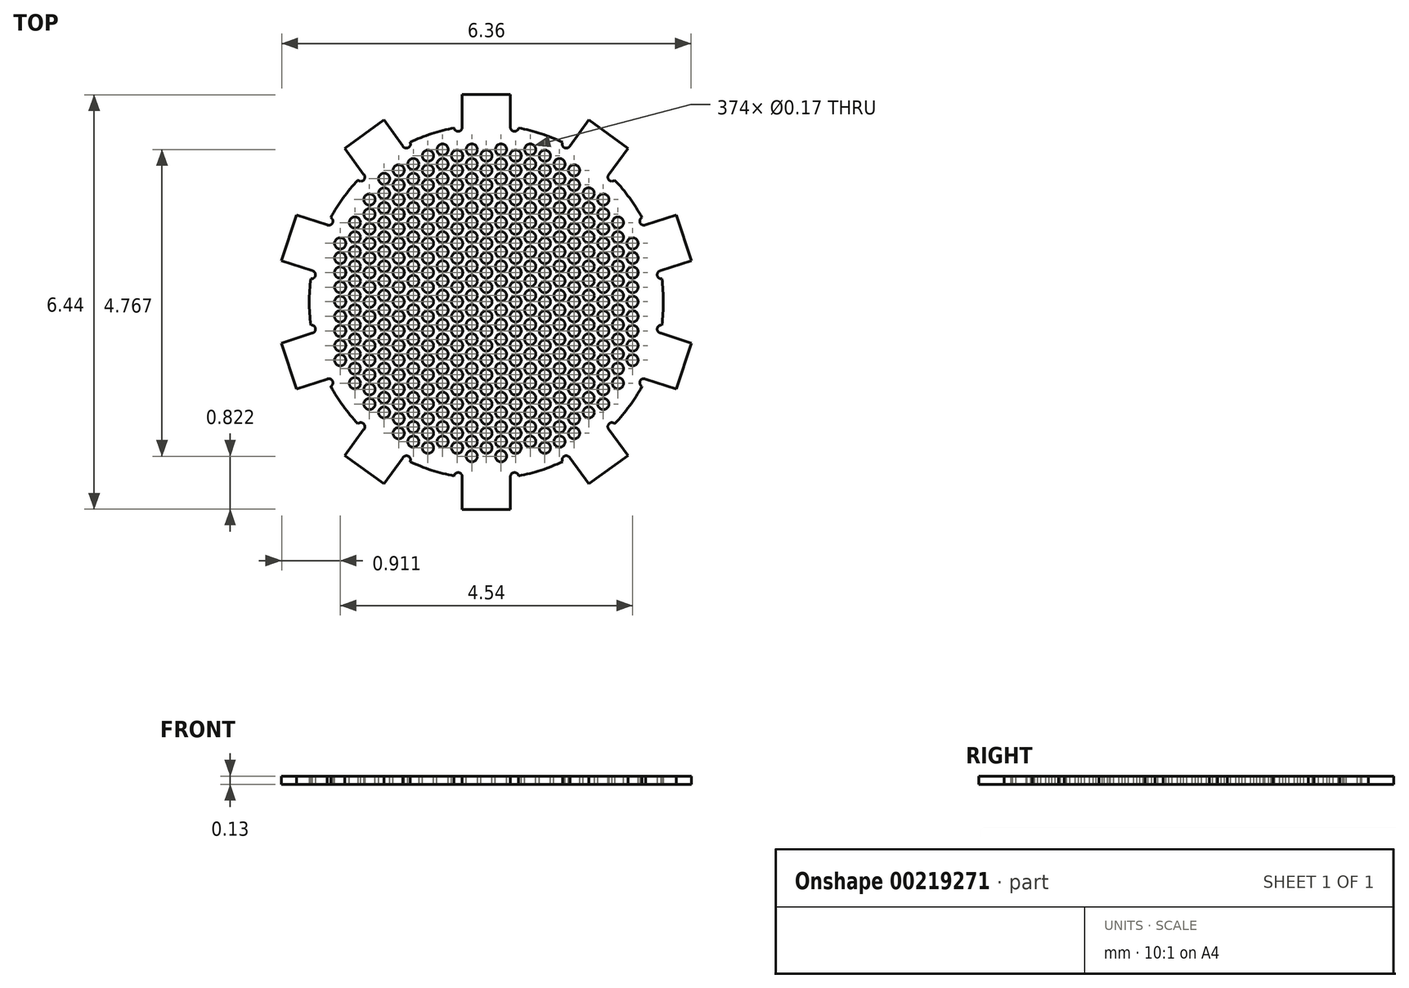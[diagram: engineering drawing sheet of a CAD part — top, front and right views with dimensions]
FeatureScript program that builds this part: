
annotation { "Feature Type Name" : "Feature", "Feature Type Description" : "" }
export const myFeature = defineFeature(function(context is Context, id is Id, definition is map)
    precondition{}
    {
        {
            var Q0;
            Q0=qCreatedBy(makeId("Top.planeOp"),FACE);
            var sketch = newSketch(context, id + "F0", { "sketchPlane" : qUnion([Q0])});
            skCircle(sketch, "E0", {"center": v(0, 0) * mm, "radius": 2.5 * mm});
            skArc(sketch, "E1", {"start": v(0.37, 2.72) * mm, "mid": v(0, 2.75) * mm, "end": v(-0.38, 2.72) * mm});
            skLineSegment(sketch, "E2", {"start": v(-0.37, 2.72) * mm, "end": v(-0.37, 3.22) * mm});
            skLineSegment(sketch, "E3", {"start": v(-0.38, 3.22) * mm, "end": v(0.38, 3.22) * mm});
            skLineSegment(sketch, "E4", {"start": v(0.38, 3.22) * mm, "end": v(0.38, 2.72) * mm});
            skArc(sketch, "E5", {"start": v(-0.5, 2.7) * mm, "mid": v(-0.43, 2.65) * mm, "end": v(-0.38, 2.72) * mm});
            skArc(sketch, "E6", {"start": v(0.38, 2.72) * mm, "mid": v(0.43, 2.65) * mm, "end": v(0.5, 2.7) * mm});
            skArc(sketch, "E7.trimOffspring", {"start": v(-0.5, 2.7) * mm, "mid": v(-0.85, 2.62) * mm, "end": v(-1.18, 2.48) * mm});
            skArc(sketch, "E8.1.0", {"start": v(-2, 1.9) * mm, "mid": v(-1.9, 1.9) * mm, "end": v(-1.9, 1.98) * mm});
            skLineSegment(sketch, "E8.1.1", {"start": v(-1.9, 1.98) * mm, "end": v(-2.2, 2.39) * mm});
            skLineSegment(sketch, "E8.1.2", {"start": v(-2.2, 2.39) * mm, "end": v(-1.6, 2.83) * mm});
            skArc(sketch, "E8.1.3", {"start": v(-1.3, 2.42) * mm, "mid": v(-1.21, 2.4) * mm, "end": v(-1.18, 2.48) * mm});
            skLineSegment(sketch, "E8.1.4", {"start": v(-1.6, 2.83) * mm, "end": v(-1.3, 2.42) * mm});
            skArc(sketch, "E8.2.0", {"start": v(-2.73, 0.36) * mm, "mid": v(-2.65, 0.41) * mm, "end": v(-2.7, 0.49) * mm});
            skLineSegment(sketch, "E8.2.1", {"start": v(-2.7, 0.49) * mm, "end": v(-3.18, 0.64) * mm});
            skLineSegment(sketch, "E8.2.2", {"start": v(-3.18, 0.64) * mm, "end": v(-2.95, 1.35) * mm});
            skArc(sketch, "E8.2.3", {"start": v(-2.48, 1.2) * mm, "mid": v(-2.4, 1.23) * mm, "end": v(-2.42, 1.31) * mm});
            skLineSegment(sketch, "E8.2.4", {"start": v(-2.95, 1.35) * mm, "end": v(-2.48, 1.2) * mm});
            skArc(sketch, "E8.3.0", {"start": v(-2.42, -1.31) * mm, "mid": v(-2.4, -1.23) * mm, "end": v(-2.48, -1.2) * mm});
            skLineSegment(sketch, "E8.3.1", {"start": v(-2.48, -1.2) * mm, "end": v(-2.95, -1.35) * mm});
            skLineSegment(sketch, "E8.3.2", {"start": v(-2.95, -1.35) * mm, "end": v(-3.18, -0.64) * mm});
            skArc(sketch, "E8.3.3", {"start": v(-2.7, -0.49) * mm, "mid": v(-2.65, -0.41) * mm, "end": v(-2.73, -0.36) * mm});
            skLineSegment(sketch, "E8.3.4", {"start": v(-3.18, -0.64) * mm, "end": v(-2.7, -0.49) * mm});
            skArc(sketch, "E8.4.0", {"start": v(-1.18, -2.48) * mm, "mid": v(-1.21, -2.4) * mm, "end": v(-1.3, -2.42) * mm});
            skLineSegment(sketch, "E8.4.1", {"start": v(-1.3, -2.42) * mm, "end": v(-1.6, -2.83) * mm});
            skLineSegment(sketch, "E8.4.2", {"start": v(-1.6, -2.83) * mm, "end": v(-2.2, -2.39) * mm});
            skArc(sketch, "E8.4.3", {"start": v(-1.9, -1.98) * mm, "mid": v(-1.9, -1.9) * mm, "end": v(-2, -1.9) * mm});
            skLineSegment(sketch, "E8.4.4", {"start": v(-2.2, -2.39) * mm, "end": v(-1.9, -1.98) * mm});
            skArc(sketch, "E8.5.0", {"start": v(0.5, -2.7) * mm, "mid": v(0.43, -2.65) * mm, "end": v(0.37, -2.72) * mm});
            skLineSegment(sketch, "E8.5.1", {"start": v(0.37, -2.72) * mm, "end": v(0.37, -3.22) * mm});
            skLineSegment(sketch, "E8.5.2", {"start": v(0.37, -3.22) * mm, "end": v(-0.38, -3.22) * mm});
            skArc(sketch, "E8.5.3", {"start": v(-0.38, -2.72) * mm, "mid": v(-0.43, -2.65) * mm, "end": v(-0.5, -2.7) * mm});
            skLineSegment(sketch, "E8.5.4", {"start": v(-0.38, -3.22) * mm, "end": v(-0.38, -2.72) * mm});
            skArc(sketch, "E8.6.0", {"start": v(2, -1.9) * mm, "mid": v(1.9, -1.9) * mm, "end": v(1.9, -1.98) * mm});
            skLineSegment(sketch, "E8.6.1", {"start": v(1.9, -1.98) * mm, "end": v(2.2, -2.39) * mm});
            skLineSegment(sketch, "E8.6.2", {"start": v(2.2, -2.39) * mm, "end": v(1.6, -2.83) * mm});
            skArc(sketch, "E8.6.3", {"start": v(1.3, -2.42) * mm, "mid": v(1.21, -2.4) * mm, "end": v(1.18, -2.48) * mm});
            skLineSegment(sketch, "E8.6.4", {"start": v(1.6, -2.83) * mm, "end": v(1.3, -2.42) * mm});
            skArc(sketch, "E8.7.0", {"start": v(2.73, -0.36) * mm, "mid": v(2.65, -0.41) * mm, "end": v(2.7, -0.49) * mm});
            skLineSegment(sketch, "E8.7.1", {"start": v(2.7, -0.49) * mm, "end": v(3.18, -0.64) * mm});
            skLineSegment(sketch, "E8.7.2", {"start": v(3.18, -0.64) * mm, "end": v(2.95, -1.35) * mm});
            skArc(sketch, "E8.7.3", {"start": v(2.48, -1.2) * mm, "mid": v(2.4, -1.23) * mm, "end": v(2.42, -1.31) * mm});
            skLineSegment(sketch, "E8.7.4", {"start": v(2.95, -1.35) * mm, "end": v(2.48, -1.2) * mm});
            skArc(sketch, "E8.8.0", {"start": v(2.42, 1.31) * mm, "mid": v(2.4, 1.23) * mm, "end": v(2.48, 1.2) * mm});
            skLineSegment(sketch, "E8.8.1", {"start": v(2.48, 1.2) * mm, "end": v(2.95, 1.35) * mm});
            skLineSegment(sketch, "E8.8.2", {"start": v(2.95, 1.35) * mm, "end": v(3.18, 0.64) * mm});
            skArc(sketch, "E8.8.3", {"start": v(2.7, 0.49) * mm, "mid": v(2.65, 0.41) * mm, "end": v(2.73, 0.36) * mm});
            skLineSegment(sketch, "E8.8.4", {"start": v(3.18, 0.64) * mm, "end": v(2.7, 0.49) * mm});
            skArc(sketch, "E8.9.0", {"start": v(1.18, 2.48) * mm, "mid": v(1.21, 2.4) * mm, "end": v(1.3, 2.42) * mm});
            skLineSegment(sketch, "E8.9.1", {"start": v(1.3, 2.42) * mm, "end": v(1.6, 2.83) * mm});
            skLineSegment(sketch, "E8.9.2", {"start": v(1.6, 2.83) * mm, "end": v(2.2, 2.39) * mm});
            skArc(sketch, "E8.9.3", {"start": v(1.9, 1.98) * mm, "mid": v(1.9, 1.9) * mm, "end": v(2, 1.9) * mm});
            skLineSegment(sketch, "E8.9.4", {"start": v(2.2, 2.39) * mm, "end": v(1.9, 1.98) * mm});
            skArc(sketch, "E9.trimOffspring", {"start": v(1.18, 2.48) * mm, "mid": v(0.85, 2.62) * mm, "end": v(0.5, 2.7) * mm});
            skArc(sketch, "E10.trimOffspring", {"start": v(1.9, 1.98) * mm, "mid": v(1.62, 2.22) * mm, "end": v(1.3, 2.42) * mm});
            skArc(sketch, "E11.trimOffspring", {"start": v(2.42, 1.31) * mm, "mid": v(2.22, 1.62) * mm, "end": v(2, 1.9) * mm});
            skArc(sketch, "E12.trimOffspring", {"start": v(2.7, 0.49) * mm, "mid": v(2.62, 0.85) * mm, "end": v(2.48, 1.2) * mm});
            skArc(sketch, "E13.trimOffspring", {"start": v(2.73, -0.36) * mm, "mid": v(2.75, 0) * mm, "end": v(2.73, 0.36) * mm});
            skArc(sketch, "E14.trimOffspring", {"start": v(2.48, -1.2) * mm, "mid": v(2.62, -0.85) * mm, "end": v(2.7, -0.49) * mm});
            skArc(sketch, "E15.trimOffspring", {"start": v(2, -1.9) * mm, "mid": v(2.22, -1.62) * mm, "end": v(2.42, -1.31) * mm});
            skArc(sketch, "E16.trimOffspring", {"start": v(1.3, -2.42) * mm, "mid": v(1.62, -2.22) * mm, "end": v(1.9, -1.98) * mm});
            skArc(sketch, "E17.trimOffspring", {"start": v(0.44, -2.71) * mm, "mid": v(0.82, -2.63) * mm, "end": v(1.18, -2.48) * mm});
            skArc(sketch, "E18.trimOffspring", {"start": v(-1.24, -2.45) * mm, "mid": v(-0.88, -2.6) * mm, "end": v(-0.5, -2.7) * mm});
            skArc(sketch, "E19.trimOffspring", {"start": v(-2.42, -1.31) * mm, "mid": v(-2.22, -1.62) * mm, "end": v(-2, -1.9) * mm});
            skArc(sketch, "E20.trimOffspring", {"start": v(-2.7, -0.49) * mm, "mid": v(-2.62, -0.85) * mm, "end": v(-2.48, -1.2) * mm});
            skArc(sketch, "E21.trimOffspring", {"start": v(-2.73, 0.36) * mm, "mid": v(-2.75, 0) * mm, "end": v(-2.73, -0.36) * mm});
            skArc(sketch, "E22.trimOffspring", {"start": v(-2.48, 1.2) * mm, "mid": v(-2.62, 0.85) * mm, "end": v(-2.7, 0.49) * mm});
            skArc(sketch, "E23.trimOffspring", {"start": v(-2, 1.9) * mm, "mid": v(-2.22, 1.62) * mm, "end": v(-2.42, 1.31) * mm});
            skArc(sketch, "E24.trimOffspring", {"start": v(-1.3, 2.42) * mm, "mid": v(-1.62, 2.22) * mm, "end": v(-1.9, 1.98) * mm});
            skSolve(sketch);
        }
        {
            var Q0;
            Q0=qSketchRegion(id+"F0",true);
            var Q1;
            Q1=makeQuery(id+"F0.imprint","IMPRINT",FACE,{"disambiguationData":[TD([[makeQuery(id+"F0.imprint","IMPRINT",EDGE,{"derivedFrom":sQuery(id+"F0.wireOp",EDGE,"E0")}),1.0]])]});
            extrude(context, id + "F1", {"entities" : qUnion([Q0, Q1]), "depth" : 0.13 * mm});
        }
        {
            var Q0;
            Q0=makeQuery(id+"F1.opExtrude","CAP_FACE",FACE,{"disambiguationData":[OSD([sQuery(id+"F0.wireOp",EDGE,"E2"),sQuery(id+"F0.wireOp",EDGE,"E3"),sQuery(id+"F0.wireOp",EDGE,"E4"),sQuery(id+"F0.wireOp",EDGE,"E5"),sQuery(id+"F0.wireOp",EDGE,"E6"),sQuery(id+"F0.wireOp",EDGE,"E7.trimOffspring")])],"isStart":false});
            cPlane(context, id + "F2", {"entities" : qUnion([Q0]), "cplaneType" : CPlaneType.OFFSET, "offset" : 0 * mm, "width" : 150 * mm, "height" : 150 * mm});
        }
        {
            var Q0;
            Q0=qCreatedBy(id+"F2.planeOp",FACE);
            var sketch = newSketch(context, id + "F3", { "sketchPlane" : qUnion([Q0])});
            skCircle(sketch, "E25.2.1.8", {"center": v(-2.04, 1.23) * mm, "radius": 0.09 * mm});
            skCircle(sketch, "E25.2.1.9", {"center": v(-2.04, 1) * mm, "radius": 0.09 * mm});
            skCircle(sketch, "E25.0.1.10", {"center": v(-2.27, 0.91) * mm, "radius": 0.09 * mm});
            skCircle(sketch, "E25.2.1.10", {"center": v(-2.04, 0.78) * mm, "radius": 0.09 * mm});
            skCircle(sketch, "E25.2.2.5", {"center": v(-1.59, 1.91) * mm, "radius": 0.09 * mm});
            skCircle(sketch, "E25.2.2.6", {"center": v(-1.59, 1.69) * mm, "radius": 0.09 * mm});
            skCircle(sketch, "E25.0.2.7", {"center": v(-1.82, 1.6) * mm, "radius": 0.09 * mm});
            skCircle(sketch, "E25.2.2.7", {"center": v(-1.59, 1.46) * mm, "radius": 0.09 * mm});
            skCircle(sketch, "E25.0.2.8", {"center": v(-1.82, 1.36) * mm, "radius": 0.09 * mm});
            skCircle(sketch, "E25.2.2.8", {"center": v(-1.59, 1.23) * mm, "radius": 0.09 * mm});
            skCircle(sketch, "E25.0.2.9", {"center": v(-1.82, 1.14) * mm, "radius": 0.09 * mm});
            skCircle(sketch, "E25.2.2.9", {"center": v(-1.59, 1) * mm, "radius": 0.09 * mm});
            skCircle(sketch, "E25.0.2.10", {"center": v(-1.82, 0.91) * mm, "radius": 0.09 * mm});
            skCircle(sketch, "E25.2.2.10", {"center": v(-1.59, 0.78) * mm, "radius": 0.09 * mm});
            skCircle(sketch, "E25.2.3.4", {"center": v(-1.13, 2.14) * mm, "radius": 0.09 * mm});
            skCircle(sketch, "E25.0.3.5", {"center": v(-1.36, 2.05) * mm, "radius": 0.09 * mm});
            skCircle(sketch, "E25.2.3.5", {"center": v(-1.13, 1.91) * mm, "radius": 0.09 * mm});
            skCircle(sketch, "E25.0.3.6", {"center": v(-1.36, 1.82) * mm, "radius": 0.09 * mm});
            skCircle(sketch, "E25.2.3.6", {"center": v(-1.13, 1.69) * mm, "radius": 0.09 * mm});
            skCircle(sketch, "E25.0.3.7", {"center": v(-1.36, 1.6) * mm, "radius": 0.09 * mm});
            skCircle(sketch, "E25.2.3.7", {"center": v(-1.13, 1.46) * mm, "radius": 0.09 * mm});
            skCircle(sketch, "E25.0.3.8", {"center": v(-1.36, 1.36) * mm, "radius": 0.09 * mm});
            skCircle(sketch, "E25.2.3.8", {"center": v(-1.13, 1.23) * mm, "radius": 0.09 * mm});
            skCircle(sketch, "E25.0.3.9", {"center": v(-1.36, 1.14) * mm, "radius": 0.09 * mm});
            skCircle(sketch, "E25.2.3.9", {"center": v(-1.13, 1) * mm, "radius": 0.09 * mm});
            skCircle(sketch, "E25.0.3.10", {"center": v(-1.36, 0.91) * mm, "radius": 0.09 * mm});
            skCircle(sketch, "E25.2.3.10", {"center": v(-1.13, 0.78) * mm, "radius": 0.09 * mm});
            skCircle(sketch, "E25.2.4.3", {"center": v(-0.68, 2.37) * mm, "radius": 0.09 * mm});
            skCircle(sketch, "E25.0.4.4", {"center": v(-0.9, 2.27) * mm, "radius": 0.09 * mm});
            skCircle(sketch, "E25.2.4.4", {"center": v(-0.68, 2.14) * mm, "radius": 0.09 * mm});
            skCircle(sketch, "E25.0.4.5", {"center": v(-0.9, 2.05) * mm, "radius": 0.09 * mm});
            skCircle(sketch, "E25.2.4.5", {"center": v(-0.68, 1.91) * mm, "radius": 0.09 * mm});
            skCircle(sketch, "E25.0.4.6", {"center": v(-0.9, 1.82) * mm, "radius": 0.09 * mm});
            skCircle(sketch, "E25.2.4.6", {"center": v(-0.68, 1.69) * mm, "radius": 0.09 * mm});
            skCircle(sketch, "E25.0.4.7", {"center": v(-0.9, 1.6) * mm, "radius": 0.09 * mm});
            skCircle(sketch, "E25.2.4.7", {"center": v(-0.68, 1.46) * mm, "radius": 0.09 * mm});
            skCircle(sketch, "E25.0.4.8", {"center": v(-0.9, 1.36) * mm, "radius": 0.09 * mm});
            skCircle(sketch, "E25.2.4.8", {"center": v(-0.68, 1.23) * mm, "radius": 0.09 * mm});
            skCircle(sketch, "E25.0.4.9", {"center": v(-0.9, 1.14) * mm, "radius": 0.09 * mm});
            skCircle(sketch, "E25.2.4.9", {"center": v(-0.68, 1) * mm, "radius": 0.09 * mm});
            skCircle(sketch, "E25.0.4.10", {"center": v(-0.9, 0.91) * mm, "radius": 0.09 * mm});
            skCircle(sketch, "E25.2.4.10", {"center": v(-0.68, 0.78) * mm, "radius": 0.09 * mm});
            skCircle(sketch, "E25.2.5.3", {"center": v(-0.23, 2.37) * mm, "radius": 0.09 * mm});
            skCircle(sketch, "E25.0.5.4", {"center": v(-0.45, 2.27) * mm, "radius": 0.09 * mm});
            skCircle(sketch, "E25.2.5.4", {"center": v(-0.23, 2.14) * mm, "radius": 0.09 * mm});
            skCircle(sketch, "E25.0.5.5", {"center": v(-0.45, 2.05) * mm, "radius": 0.09 * mm});
            skCircle(sketch, "E25.2.5.5", {"center": v(-0.23, 1.91) * mm, "radius": 0.09 * mm});
            skCircle(sketch, "E25.0.5.6", {"center": v(-0.45, 1.82) * mm, "radius": 0.09 * mm});
            skCircle(sketch, "E25.2.5.6", {"center": v(-0.23, 1.69) * mm, "radius": 0.09 * mm});
            skCircle(sketch, "E25.0.5.7", {"center": v(-0.45, 1.6) * mm, "radius": 0.09 * mm});
            skCircle(sketch, "E25.2.5.7", {"center": v(-0.23, 1.46) * mm, "radius": 0.09 * mm});
            skCircle(sketch, "E25.0.5.8", {"center": v(-0.45, 1.36) * mm, "radius": 0.09 * mm});
            skCircle(sketch, "E25.2.5.8", {"center": v(-0.23, 1.23) * mm, "radius": 0.09 * mm});
            skCircle(sketch, "E25.0.5.9", {"center": v(-0.45, 1.14) * mm, "radius": 0.09 * mm});
            skCircle(sketch, "E25.2.5.9", {"center": v(-0.23, 1) * mm, "radius": 0.09 * mm});
            skCircle(sketch, "E25.0.5.10", {"center": v(-0.45, 0.91) * mm, "radius": 0.09 * mm});
            skCircle(sketch, "E25.2.5.10", {"center": v(-0.23, 0.78) * mm, "radius": 0.09 * mm});
            skCircle(sketch, "E25.2.6.3", {"center": v(0.23, 2.37) * mm, "radius": 0.09 * mm});
            skCircle(sketch, "E25.0.6.4", {"center": v(0, 2.27) * mm, "radius": 0.09 * mm});
            skCircle(sketch, "E25.2.6.4", {"center": v(0.23, 2.14) * mm, "radius": 0.09 * mm});
            skCircle(sketch, "E25.0.6.5", {"center": v(0, 2.05) * mm, "radius": 0.09 * mm});
            skCircle(sketch, "E25.2.6.5", {"center": v(0.23, 1.91) * mm, "radius": 0.09 * mm});
            skCircle(sketch, "E25.0.6.6", {"center": v(0, 1.82) * mm, "radius": 0.09 * mm});
            skCircle(sketch, "E25.2.6.6", {"center": v(0.23, 1.69) * mm, "radius": 0.09 * mm});
            skCircle(sketch, "E25.0.6.7", {"center": v(0, 1.6) * mm, "radius": 0.09 * mm});
            skCircle(sketch, "E25.2.6.7", {"center": v(0.23, 1.46) * mm, "radius": 0.09 * mm});
            skCircle(sketch, "E25.0.6.8", {"center": v(0, 1.36) * mm, "radius": 0.09 * mm});
            skCircle(sketch, "E25.2.6.8", {"center": v(0.23, 1.23) * mm, "radius": 0.09 * mm});
            skCircle(sketch, "E25.0.6.9", {"center": v(0, 1.14) * mm, "radius": 0.09 * mm});
            skCircle(sketch, "E25.2.6.9", {"center": v(0.23, 1) * mm, "radius": 0.09 * mm});
            skCircle(sketch, "E25.0.6.10", {"center": v(0, 0.91) * mm, "radius": 0.09 * mm});
            skCircle(sketch, "E25.2.6.10", {"center": v(0.23, 0.78) * mm, "radius": 0.09 * mm});
            skCircle(sketch, "E25.2.7.3", {"center": v(0.68, 2.37) * mm, "radius": 0.09 * mm});
            skCircle(sketch, "E25.0.7.4", {"center": v(0.45, 2.27) * mm, "radius": 0.09 * mm});
            skCircle(sketch, "E25.2.7.4", {"center": v(0.68, 2.14) * mm, "radius": 0.09 * mm});
            skCircle(sketch, "E25.0.7.5", {"center": v(0.45, 2.05) * mm, "radius": 0.09 * mm});
            skCircle(sketch, "E25.2.7.5", {"center": v(0.68, 1.91) * mm, "radius": 0.09 * mm});
            skCircle(sketch, "E25.0.7.6", {"center": v(0.45, 1.82) * mm, "radius": 0.09 * mm});
            skCircle(sketch, "E25.2.7.6", {"center": v(0.68, 1.69) * mm, "radius": 0.09 * mm});
            skCircle(sketch, "E25.0.7.7", {"center": v(0.45, 1.6) * mm, "radius": 0.09 * mm});
            skCircle(sketch, "E25.2.7.7", {"center": v(0.68, 1.46) * mm, "radius": 0.09 * mm});
            skCircle(sketch, "E25.0.7.8", {"center": v(0.45, 1.36) * mm, "radius": 0.09 * mm});
            skCircle(sketch, "E25.2.7.8", {"center": v(0.68, 1.23) * mm, "radius": 0.09 * mm});
            skCircle(sketch, "E25.0.7.9", {"center": v(0.45, 1.14) * mm, "radius": 0.09 * mm});
            skCircle(sketch, "E25.2.7.9", {"center": v(0.68, 1) * mm, "radius": 0.09 * mm});
            skCircle(sketch, "E25.0.7.10", {"center": v(0.45, 0.91) * mm, "radius": 0.09 * mm});
            skCircle(sketch, "E25.2.7.10", {"center": v(0.68, 0.78) * mm, "radius": 0.09 * mm});
            skCircle(sketch, "E25.0.8.4", {"center": v(0.9, 2.27) * mm, "radius": 0.09 * mm});
            skCircle(sketch, "E25.2.8.4", {"center": v(1.14, 2.14) * mm, "radius": 0.09 * mm});
            skCircle(sketch, "E25.0.8.5", {"center": v(0.9, 2.05) * mm, "radius": 0.09 * mm});
            skCircle(sketch, "E25.2.8.5", {"center": v(1.14, 1.91) * mm, "radius": 0.09 * mm});
            skCircle(sketch, "E25.0.8.6", {"center": v(0.9, 1.82) * mm, "radius": 0.09 * mm});
            skCircle(sketch, "E25.2.8.6", {"center": v(1.14, 1.69) * mm, "radius": 0.09 * mm});
            skCircle(sketch, "E25.0.8.7", {"center": v(0.9, 1.6) * mm, "radius": 0.09 * mm});
            skCircle(sketch, "E25.2.8.7", {"center": v(1.14, 1.46) * mm, "radius": 0.09 * mm});
            skCircle(sketch, "E25.0.8.8", {"center": v(0.9, 1.36) * mm, "radius": 0.09 * mm});
            skCircle(sketch, "E25.2.8.8", {"center": v(1.14, 1.23) * mm, "radius": 0.09 * mm});
            skCircle(sketch, "E25.0.8.9", {"center": v(0.9, 1.14) * mm, "radius": 0.09 * mm});
            skCircle(sketch, "E25.2.8.9", {"center": v(1.14, 1) * mm, "radius": 0.09 * mm});
            skCircle(sketch, "E25.0.8.10", {"center": v(0.9, 0.91) * mm, "radius": 0.09 * mm});
            skCircle(sketch, "E25.2.8.10", {"center": v(1.14, 0.78) * mm, "radius": 0.09 * mm});
            skCircle(sketch, "E25.0.9.5", {"center": v(1.36, 2.05) * mm, "radius": 0.09 * mm});
            skCircle(sketch, "E25.0.9.6", {"center": v(1.36, 1.82) * mm, "radius": 0.09 * mm});
            skCircle(sketch, "E25.2.9.6", {"center": v(1.6, 1.69) * mm, "radius": 0.09 * mm});
            skCircle(sketch, "E25.0.9.7", {"center": v(1.36, 1.6) * mm, "radius": 0.09 * mm});
            skCircle(sketch, "E25.2.9.7", {"center": v(1.6, 1.46) * mm, "radius": 0.09 * mm});
            skCircle(sketch, "E25.0.9.8", {"center": v(1.36, 1.36) * mm, "radius": 0.09 * mm});
            skCircle(sketch, "E25.2.9.8", {"center": v(1.6, 1.23) * mm, "radius": 0.09 * mm});
            skCircle(sketch, "E25.0.9.9", {"center": v(1.36, 1.14) * mm, "radius": 0.09 * mm});
            skCircle(sketch, "E25.2.9.9", {"center": v(1.6, 1) * mm, "radius": 0.09 * mm});
            skCircle(sketch, "E25.0.9.10", {"center": v(1.36, 0.91) * mm, "radius": 0.09 * mm});
            skCircle(sketch, "E25.2.9.10", {"center": v(1.6, 0.78) * mm, "radius": 0.09 * mm});
            skCircle(sketch, "E25.0.10.7", {"center": v(1.82, 1.6) * mm, "radius": 0.09 * mm});
            skCircle(sketch, "E25.0.10.8", {"center": v(1.82, 1.36) * mm, "radius": 0.09 * mm});
            skCircle(sketch, "E25.2.10.8", {"center": v(2.04, 1.23) * mm, "radius": 0.09 * mm});
            skCircle(sketch, "E25.0.10.9", {"center": v(1.82, 1.14) * mm, "radius": 0.09 * mm});
            skCircle(sketch, "E25.2.10.9", {"center": v(2.04, 1) * mm, "radius": 0.09 * mm});
            skCircle(sketch, "E25.0.10.10", {"center": v(1.82, 0.91) * mm, "radius": 0.09 * mm});
            skCircle(sketch, "E25.2.10.10", {"center": v(2.04, 0.78) * mm, "radius": 0.09 * mm});
            skCircle(sketch, "E26.0.1.11", {"center": v(-2.27, 0.68) * mm, "radius": 0.09 * mm});
            skCircle(sketch, "E26.2.1.11", {"center": v(-2.04, 0.55) * mm, "radius": 0.09 * mm});
            skCircle(sketch, "E26.0.1.12", {"center": v(-2.27, 0.46) * mm, "radius": 0.09 * mm});
            skCircle(sketch, "E26.2.1.12", {"center": v(-2.04, 0.33) * mm, "radius": 0.09 * mm});
            skCircle(sketch, "E26.0.1.13", {"center": v(-2.27, 0.23) * mm, "radius": 0.09 * mm});
            skCircle(sketch, "E26.2.1.13", {"center": v(-2.04, 0.1) * mm, "radius": 0.09 * mm});
            skCircle(sketch, "E26.0.1.14", {"center": v(-2.27, 0) * mm, "radius": 0.09 * mm});
            skCircle(sketch, "E26.2.1.14", {"center": v(-2.04, -0.13) * mm, "radius": 0.09 * mm});
            skCircle(sketch, "E26.0.1.15", {"center": v(-2.27, -0.22) * mm, "radius": 0.09 * mm});
            skCircle(sketch, "E26.2.1.15", {"center": v(-2.04, -0.36) * mm, "radius": 0.09 * mm});
            skCircle(sketch, "E26.0.1.16", {"center": v(-2.27, -0.45) * mm, "radius": 0.09 * mm});
            skCircle(sketch, "E26.2.1.16", {"center": v(-2.04, -0.58) * mm, "radius": 0.09 * mm});
            skCircle(sketch, "E26.0.1.17", {"center": v(-2.27, -0.68) * mm, "radius": 0.09 * mm});
            skCircle(sketch, "E26.2.1.17", {"center": v(-2.04, -0.8) * mm, "radius": 0.09 * mm});
            skCircle(sketch, "E26.0.1.18", {"center": v(-2.27, -0.9) * mm, "radius": 0.09 * mm});
            skCircle(sketch, "E26.2.1.18", {"center": v(-2.04, -1.04) * mm, "radius": 0.09 * mm});
            skCircle(sketch, "E26.2.1.19", {"center": v(-2.04, -1.26) * mm, "radius": 0.09 * mm});
            skCircle(sketch, "E26.0.2.11", {"center": v(-1.82, 0.68) * mm, "radius": 0.09 * mm});
            skCircle(sketch, "E26.2.2.11", {"center": v(-1.59, 0.55) * mm, "radius": 0.09 * mm});
            skCircle(sketch, "E26.0.2.12", {"center": v(-1.82, 0.46) * mm, "radius": 0.09 * mm});
            skCircle(sketch, "E26.2.2.12", {"center": v(-1.59, 0.33) * mm, "radius": 0.09 * mm});
            skCircle(sketch, "E26.0.2.13", {"center": v(-1.82, 0.23) * mm, "radius": 0.09 * mm});
            skCircle(sketch, "E26.2.2.13", {"center": v(-1.59, 0.1) * mm, "radius": 0.09 * mm});
            skCircle(sketch, "E26.0.2.14", {"center": v(-1.82, 0) * mm, "radius": 0.09 * mm});
            skCircle(sketch, "E26.2.2.14", {"center": v(-1.59, -0.13) * mm, "radius": 0.09 * mm});
            skCircle(sketch, "E26.0.2.15", {"center": v(-1.82, -0.22) * mm, "radius": 0.09 * mm});
            skCircle(sketch, "E26.2.2.15", {"center": v(-1.59, -0.36) * mm, "radius": 0.09 * mm});
            skCircle(sketch, "E26.0.2.16", {"center": v(-1.82, -0.45) * mm, "radius": 0.09 * mm});
            skCircle(sketch, "E26.2.2.16", {"center": v(-1.59, -0.58) * mm, "radius": 0.09 * mm});
            skCircle(sketch, "E26.0.2.17", {"center": v(-1.82, -0.68) * mm, "radius": 0.09 * mm});
            skCircle(sketch, "E26.2.2.17", {"center": v(-1.59, -0.8) * mm, "radius": 0.09 * mm});
            skCircle(sketch, "E26.0.2.18", {"center": v(-1.82, -0.9) * mm, "radius": 0.09 * mm});
            skCircle(sketch, "E26.2.2.18", {"center": v(-1.59, -1.04) * mm, "radius": 0.09 * mm});
            skCircle(sketch, "E26.0.2.19", {"center": v(-1.82, -1.13) * mm, "radius": 0.09 * mm});
            skCircle(sketch, "E26.2.2.19", {"center": v(-1.59, -1.26) * mm, "radius": 0.09 * mm});
            skCircle(sketch, "E26.0.2.20", {"center": v(-1.82, -1.36) * mm, "radius": 0.09 * mm});
            skCircle(sketch, "E26.2.2.20", {"center": v(-1.59, -1.5) * mm, "radius": 0.09 * mm});
            skCircle(sketch, "E26.0.2.21", {"center": v(-1.82, -1.59) * mm, "radius": 0.09 * mm});
            skCircle(sketch, "E26.2.2.21", {"center": v(-1.59, -1.72) * mm, "radius": 0.09 * mm});
            skCircle(sketch, "E26.0.3.11", {"center": v(-1.36, 0.68) * mm, "radius": 0.09 * mm});
            skCircle(sketch, "E26.2.3.11", {"center": v(-1.13, 0.55) * mm, "radius": 0.09 * mm});
            skCircle(sketch, "E26.0.3.12", {"center": v(-1.36, 0.46) * mm, "radius": 0.09 * mm});
            skCircle(sketch, "E26.2.3.12", {"center": v(-1.13, 0.33) * mm, "radius": 0.09 * mm});
            skCircle(sketch, "E26.0.3.13", {"center": v(-1.36, 0.23) * mm, "radius": 0.09 * mm});
            skCircle(sketch, "E26.2.3.13", {"center": v(-1.13, 0.1) * mm, "radius": 0.09 * mm});
            skCircle(sketch, "E26.0.3.14", {"center": v(-1.36, 0) * mm, "radius": 0.09 * mm});
            skCircle(sketch, "E26.2.3.14", {"center": v(-1.13, -0.13) * mm, "radius": 0.09 * mm});
            skCircle(sketch, "E26.0.3.15", {"center": v(-1.36, -0.22) * mm, "radius": 0.09 * mm});
            skCircle(sketch, "E26.2.3.15", {"center": v(-1.13, -0.36) * mm, "radius": 0.09 * mm});
            skCircle(sketch, "E26.0.3.16", {"center": v(-1.36, -0.45) * mm, "radius": 0.09 * mm});
            skCircle(sketch, "E26.2.3.16", {"center": v(-1.13, -0.58) * mm, "radius": 0.09 * mm});
            skCircle(sketch, "E26.0.3.17", {"center": v(-1.36, -0.68) * mm, "radius": 0.09 * mm});
            skCircle(sketch, "E26.2.3.17", {"center": v(-1.13, -0.8) * mm, "radius": 0.09 * mm});
            skCircle(sketch, "E26.0.3.18", {"center": v(-1.36, -0.9) * mm, "radius": 0.09 * mm});
            skCircle(sketch, "E26.2.3.18", {"center": v(-1.13, -1.04) * mm, "radius": 0.09 * mm});
            skCircle(sketch, "E26.0.3.19", {"center": v(-1.36, -1.13) * mm, "radius": 0.09 * mm});
            skCircle(sketch, "E26.2.3.19", {"center": v(-1.13, -1.26) * mm, "radius": 0.09 * mm});
            skCircle(sketch, "E26.0.3.20", {"center": v(-1.36, -1.36) * mm, "radius": 0.09 * mm});
            skCircle(sketch, "E26.2.3.20", {"center": v(-1.13, -1.5) * mm, "radius": 0.09 * mm});
            skCircle(sketch, "E26.0.3.21", {"center": v(-1.36, -1.59) * mm, "radius": 0.09 * mm});
            skCircle(sketch, "E26.2.3.21", {"center": v(-1.13, -1.72) * mm, "radius": 0.09 * mm});
            skCircle(sketch, "E26.0.4.11", {"center": v(-0.9, 0.68) * mm, "radius": 0.09 * mm});
            skCircle(sketch, "E26.2.4.11", {"center": v(-0.68, 0.55) * mm, "radius": 0.09 * mm});
            skCircle(sketch, "E26.0.4.12", {"center": v(-0.9, 0.46) * mm, "radius": 0.09 * mm});
            skCircle(sketch, "E26.2.4.12", {"center": v(-0.68, 0.33) * mm, "radius": 0.09 * mm});
            skCircle(sketch, "E26.0.4.13", {"center": v(-0.9, 0.23) * mm, "radius": 0.09 * mm});
            skCircle(sketch, "E26.2.4.13", {"center": v(-0.68, 0.1) * mm, "radius": 0.09 * mm});
            skCircle(sketch, "E26.0.4.14", {"center": v(-0.9, 0) * mm, "radius": 0.09 * mm});
            skCircle(sketch, "E26.2.4.14", {"center": v(-0.68, -0.13) * mm, "radius": 0.09 * mm});
            skCircle(sketch, "E26.0.4.15", {"center": v(-0.9, -0.22) * mm, "radius": 0.09 * mm});
            skCircle(sketch, "E26.2.4.15", {"center": v(-0.68, -0.36) * mm, "radius": 0.09 * mm});
            skCircle(sketch, "E26.0.4.16", {"center": v(-0.9, -0.45) * mm, "radius": 0.09 * mm});
            skCircle(sketch, "E26.2.4.16", {"center": v(-0.68, -0.58) * mm, "radius": 0.09 * mm});
            skCircle(sketch, "E26.0.4.17", {"center": v(-0.9, -0.68) * mm, "radius": 0.09 * mm});
            skCircle(sketch, "E26.2.4.17", {"center": v(-0.68, -0.8) * mm, "radius": 0.09 * mm});
            skCircle(sketch, "E26.0.4.18", {"center": v(-0.9, -0.9) * mm, "radius": 0.09 * mm});
            skCircle(sketch, "E26.2.4.18", {"center": v(-0.68, -1.04) * mm, "radius": 0.09 * mm});
            skCircle(sketch, "E26.0.4.19", {"center": v(-0.9, -1.13) * mm, "radius": 0.09 * mm});
            skCircle(sketch, "E26.2.4.19", {"center": v(-0.68, -1.26) * mm, "radius": 0.09 * mm});
            skCircle(sketch, "E26.0.4.20", {"center": v(-0.9, -1.36) * mm, "radius": 0.09 * mm});
            skCircle(sketch, "E26.2.4.20", {"center": v(-0.68, -1.5) * mm, "radius": 0.09 * mm});
            skCircle(sketch, "E26.0.4.21", {"center": v(-0.9, -1.59) * mm, "radius": 0.09 * mm});
            skCircle(sketch, "E26.2.4.21", {"center": v(-0.68, -1.72) * mm, "radius": 0.09 * mm});
            skCircle(sketch, "E26.0.5.11", {"center": v(-0.45, 0.68) * mm, "radius": 0.09 * mm});
            skCircle(sketch, "E26.2.5.11", {"center": v(-0.23, 0.55) * mm, "radius": 0.09 * mm});
            skCircle(sketch, "E26.0.5.12", {"center": v(-0.45, 0.46) * mm, "radius": 0.09 * mm});
            skCircle(sketch, "E26.2.5.12", {"center": v(-0.23, 0.33) * mm, "radius": 0.09 * mm});
            skCircle(sketch, "E26.0.5.13", {"center": v(-0.45, 0.23) * mm, "radius": 0.09 * mm});
            skCircle(sketch, "E26.2.5.13", {"center": v(-0.23, 0.1) * mm, "radius": 0.09 * mm});
            skCircle(sketch, "E26.0.5.14", {"center": v(-0.45, 0) * mm, "radius": 0.09 * mm});
            skCircle(sketch, "E26.2.5.14", {"center": v(-0.23, -0.13) * mm, "radius": 0.09 * mm});
            skCircle(sketch, "E26.0.5.15", {"center": v(-0.45, -0.22) * mm, "radius": 0.09 * mm});
            skCircle(sketch, "E26.2.5.15", {"center": v(-0.23, -0.36) * mm, "radius": 0.09 * mm});
            skCircle(sketch, "E26.0.5.16", {"center": v(-0.45, -0.45) * mm, "radius": 0.09 * mm});
            skCircle(sketch, "E26.2.5.16", {"center": v(-0.23, -0.58) * mm, "radius": 0.09 * mm});
            skCircle(sketch, "E26.0.5.17", {"center": v(-0.45, -0.68) * mm, "radius": 0.09 * mm});
            skCircle(sketch, "E26.2.5.17", {"center": v(-0.23, -0.8) * mm, "radius": 0.09 * mm});
            skCircle(sketch, "E26.0.5.18", {"center": v(-0.45, -0.9) * mm, "radius": 0.09 * mm});
            skCircle(sketch, "E26.2.5.18", {"center": v(-0.23, -1.04) * mm, "radius": 0.09 * mm});
            skCircle(sketch, "E26.0.5.19", {"center": v(-0.45, -1.13) * mm, "radius": 0.09 * mm});
            skCircle(sketch, "E26.2.5.19", {"center": v(-0.23, -1.26) * mm, "radius": 0.09 * mm});
            skCircle(sketch, "E26.0.5.20", {"center": v(-0.45, -1.36) * mm, "radius": 0.09 * mm});
            skCircle(sketch, "E26.2.5.20", {"center": v(-0.23, -1.5) * mm, "radius": 0.09 * mm});
            skCircle(sketch, "E26.0.5.21", {"center": v(-0.45, -1.59) * mm, "radius": 0.09 * mm});
            skCircle(sketch, "E26.2.5.21", {"center": v(-0.23, -1.72) * mm, "radius": 0.09 * mm});
            skCircle(sketch, "E26.0.6.11", {"center": v(0, 0.68) * mm, "radius": 0.09 * mm});
            skCircle(sketch, "E26.2.6.11", {"center": v(0.23, 0.55) * mm, "radius": 0.09 * mm});
            skCircle(sketch, "E26.0.6.12", {"center": v(0, 0.46) * mm, "radius": 0.09 * mm});
            skCircle(sketch, "E26.2.6.12", {"center": v(0.23, 0.33) * mm, "radius": 0.09 * mm});
            skCircle(sketch, "E26.0.6.13", {"center": v(0, 0.23) * mm, "radius": 0.09 * mm});
            skCircle(sketch, "E26.2.6.13", {"center": v(0.23, 0.1) * mm, "radius": 0.09 * mm});
            skCircle(sketch, "E26.0.6.14", {"center": v(0, 0) * mm, "radius": 0.09 * mm});
            skCircle(sketch, "E26.2.6.14", {"center": v(0.23, -0.13) * mm, "radius": 0.09 * mm});
            skCircle(sketch, "E26.0.6.15", {"center": v(0, -0.22) * mm, "radius": 0.09 * mm});
            skCircle(sketch, "E26.2.6.15", {"center": v(0.23, -0.36) * mm, "radius": 0.09 * mm});
            skCircle(sketch, "E26.0.6.16", {"center": v(0, -0.45) * mm, "radius": 0.09 * mm});
            skCircle(sketch, "E26.2.6.16", {"center": v(0.23, -0.58) * mm, "radius": 0.09 * mm});
            skCircle(sketch, "E26.0.6.17", {"center": v(0, -0.68) * mm, "radius": 0.09 * mm});
            skCircle(sketch, "E26.2.6.17", {"center": v(0.23, -0.8) * mm, "radius": 0.09 * mm});
            skCircle(sketch, "E26.0.6.18", {"center": v(0, -0.9) * mm, "radius": 0.09 * mm});
            skCircle(sketch, "E26.2.6.18", {"center": v(0.23, -1.04) * mm, "radius": 0.09 * mm});
            skCircle(sketch, "E26.0.6.19", {"center": v(0, -1.13) * mm, "radius": 0.09 * mm});
            skCircle(sketch, "E26.2.6.19", {"center": v(0.23, -1.26) * mm, "radius": 0.09 * mm});
            skCircle(sketch, "E26.0.6.20", {"center": v(0, -1.36) * mm, "radius": 0.09 * mm});
            skCircle(sketch, "E26.2.6.20", {"center": v(0.23, -1.5) * mm, "radius": 0.09 * mm});
            skCircle(sketch, "E26.0.6.21", {"center": v(0, -1.59) * mm, "radius": 0.09 * mm});
            skCircle(sketch, "E26.2.6.21", {"center": v(0.23, -1.72) * mm, "radius": 0.09 * mm});
            skCircle(sketch, "E26.0.7.11", {"center": v(0.45, 0.68) * mm, "radius": 0.09 * mm});
            skCircle(sketch, "E26.2.7.11", {"center": v(0.68, 0.55) * mm, "radius": 0.09 * mm});
            skCircle(sketch, "E26.0.7.12", {"center": v(0.45, 0.46) * mm, "radius": 0.09 * mm});
            skCircle(sketch, "E26.2.7.12", {"center": v(0.68, 0.33) * mm, "radius": 0.09 * mm});
            skCircle(sketch, "E26.0.7.13", {"center": v(0.45, 0.23) * mm, "radius": 0.09 * mm});
            skCircle(sketch, "E26.2.7.13", {"center": v(0.68, 0.1) * mm, "radius": 0.09 * mm});
            skCircle(sketch, "E26.0.7.14", {"center": v(0.45, 0) * mm, "radius": 0.09 * mm});
            skCircle(sketch, "E26.2.7.14", {"center": v(0.68, -0.13) * mm, "radius": 0.09 * mm});
            skCircle(sketch, "E26.0.7.15", {"center": v(0.45, -0.22) * mm, "radius": 0.09 * mm});
            skCircle(sketch, "E26.2.7.15", {"center": v(0.68, -0.36) * mm, "radius": 0.09 * mm});
            skCircle(sketch, "E26.0.7.16", {"center": v(0.45, -0.45) * mm, "radius": 0.09 * mm});
            skCircle(sketch, "E26.2.7.16", {"center": v(0.68, -0.58) * mm, "radius": 0.09 * mm});
            skCircle(sketch, "E26.0.7.17", {"center": v(0.45, -0.68) * mm, "radius": 0.09 * mm});
            skCircle(sketch, "E26.2.7.17", {"center": v(0.68, -0.8) * mm, "radius": 0.09 * mm});
            skCircle(sketch, "E26.0.7.18", {"center": v(0.45, -0.9) * mm, "radius": 0.09 * mm});
            skCircle(sketch, "E26.2.7.18", {"center": v(0.68, -1.04) * mm, "radius": 0.09 * mm});
            skCircle(sketch, "E26.0.7.19", {"center": v(0.45, -1.13) * mm, "radius": 0.09 * mm});
            skCircle(sketch, "E26.2.7.19", {"center": v(0.68, -1.26) * mm, "radius": 0.09 * mm});
            skCircle(sketch, "E26.0.7.20", {"center": v(0.45, -1.36) * mm, "radius": 0.09 * mm});
            skCircle(sketch, "E26.2.7.20", {"center": v(0.68, -1.5) * mm, "radius": 0.09 * mm});
            skCircle(sketch, "E26.0.7.21", {"center": v(0.45, -1.59) * mm, "radius": 0.09 * mm});
            skCircle(sketch, "E26.2.7.21", {"center": v(0.68, -1.72) * mm, "radius": 0.09 * mm});
            skCircle(sketch, "E26.0.8.11", {"center": v(0.9, 0.68) * mm, "radius": 0.09 * mm});
            skCircle(sketch, "E26.2.8.11", {"center": v(1.14, 0.55) * mm, "radius": 0.09 * mm});
            skCircle(sketch, "E26.0.8.12", {"center": v(0.9, 0.46) * mm, "radius": 0.09 * mm});
            skCircle(sketch, "E26.2.8.12", {"center": v(1.14, 0.33) * mm, "radius": 0.09 * mm});
            skCircle(sketch, "E26.0.8.13", {"center": v(0.9, 0.23) * mm, "radius": 0.09 * mm});
            skCircle(sketch, "E26.2.8.13", {"center": v(1.14, 0.1) * mm, "radius": 0.09 * mm});
            skCircle(sketch, "E26.0.8.14", {"center": v(0.9, 0) * mm, "radius": 0.09 * mm});
            skCircle(sketch, "E26.2.8.14", {"center": v(1.14, -0.13) * mm, "radius": 0.09 * mm});
            skCircle(sketch, "E26.0.8.15", {"center": v(0.9, -0.22) * mm, "radius": 0.09 * mm});
            skCircle(sketch, "E26.2.8.15", {"center": v(1.14, -0.36) * mm, "radius": 0.09 * mm});
            skCircle(sketch, "E26.0.8.16", {"center": v(0.9, -0.45) * mm, "radius": 0.09 * mm});
            skCircle(sketch, "E26.2.8.16", {"center": v(1.14, -0.58) * mm, "radius": 0.09 * mm});
            skCircle(sketch, "E26.0.8.17", {"center": v(0.9, -0.68) * mm, "radius": 0.09 * mm});
            skCircle(sketch, "E26.2.8.17", {"center": v(1.14, -0.8) * mm, "radius": 0.09 * mm});
            skCircle(sketch, "E26.0.8.18", {"center": v(0.9, -0.9) * mm, "radius": 0.09 * mm});
            skCircle(sketch, "E26.2.8.18", {"center": v(1.14, -1.04) * mm, "radius": 0.09 * mm});
            skCircle(sketch, "E26.0.8.19", {"center": v(0.9, -1.13) * mm, "radius": 0.09 * mm});
            skCircle(sketch, "E26.2.8.19", {"center": v(1.14, -1.26) * mm, "radius": 0.09 * mm});
            skCircle(sketch, "E26.0.8.20", {"center": v(0.9, -1.36) * mm, "radius": 0.09 * mm});
            skCircle(sketch, "E26.2.8.20", {"center": v(1.14, -1.5) * mm, "radius": 0.09 * mm});
            skCircle(sketch, "E26.0.8.21", {"center": v(0.9, -1.59) * mm, "radius": 0.09 * mm});
            skCircle(sketch, "E26.2.8.21", {"center": v(1.14, -1.72) * mm, "radius": 0.09 * mm});
            skCircle(sketch, "E26.0.9.11", {"center": v(1.36, 0.68) * mm, "radius": 0.09 * mm});
            skCircle(sketch, "E26.2.9.11", {"center": v(1.6, 0.55) * mm, "radius": 0.09 * mm});
            skCircle(sketch, "E26.0.9.12", {"center": v(1.36, 0.46) * mm, "radius": 0.09 * mm});
            skCircle(sketch, "E26.2.9.12", {"center": v(1.6, 0.33) * mm, "radius": 0.09 * mm});
            skCircle(sketch, "E26.0.9.13", {"center": v(1.36, 0.23) * mm, "radius": 0.09 * mm});
            skCircle(sketch, "E26.2.9.13", {"center": v(1.6, 0.1) * mm, "radius": 0.09 * mm});
            skCircle(sketch, "E26.0.9.14", {"center": v(1.36, 0) * mm, "radius": 0.09 * mm});
            skCircle(sketch, "E26.2.9.14", {"center": v(1.6, -0.13) * mm, "radius": 0.09 * mm});
            skCircle(sketch, "E26.0.9.15", {"center": v(1.36, -0.22) * mm, "radius": 0.09 * mm});
            skCircle(sketch, "E26.2.9.15", {"center": v(1.6, -0.36) * mm, "radius": 0.09 * mm});
            skCircle(sketch, "E26.0.9.16", {"center": v(1.36, -0.45) * mm, "radius": 0.09 * mm});
            skCircle(sketch, "E26.2.9.16", {"center": v(1.6, -0.58) * mm, "radius": 0.09 * mm});
            skCircle(sketch, "E26.0.9.17", {"center": v(1.36, -0.68) * mm, "radius": 0.09 * mm});
            skCircle(sketch, "E26.2.9.17", {"center": v(1.6, -0.8) * mm, "radius": 0.09 * mm});
            skCircle(sketch, "E26.0.9.18", {"center": v(1.36, -0.9) * mm, "radius": 0.09 * mm});
            skCircle(sketch, "E26.2.9.18", {"center": v(1.6, -1.04) * mm, "radius": 0.09 * mm});
            skCircle(sketch, "E26.0.9.19", {"center": v(1.36, -1.13) * mm, "radius": 0.09 * mm});
            skCircle(sketch, "E26.2.9.19", {"center": v(1.6, -1.26) * mm, "radius": 0.09 * mm});
            skCircle(sketch, "E26.0.9.20", {"center": v(1.36, -1.36) * mm, "radius": 0.09 * mm});
            skCircle(sketch, "E26.2.9.20", {"center": v(1.6, -1.5) * mm, "radius": 0.09 * mm});
            skCircle(sketch, "E26.0.9.21", {"center": v(1.36, -1.59) * mm, "radius": 0.09 * mm});
            skCircle(sketch, "E26.2.9.21", {"center": v(1.6, -1.72) * mm, "radius": 0.09 * mm});
            skCircle(sketch, "E26.0.10.11", {"center": v(1.82, 0.68) * mm, "radius": 0.09 * mm});
            skCircle(sketch, "E26.2.10.11", {"center": v(2.04, 0.55) * mm, "radius": 0.09 * mm});
            skCircle(sketch, "E26.0.10.12", {"center": v(1.82, 0.46) * mm, "radius": 0.09 * mm});
            skCircle(sketch, "E26.2.10.12", {"center": v(2.04, 0.33) * mm, "radius": 0.09 * mm});
            skCircle(sketch, "E26.0.10.13", {"center": v(1.82, 0.23) * mm, "radius": 0.09 * mm});
            skCircle(sketch, "E26.2.10.13", {"center": v(2.04, 0.1) * mm, "radius": 0.09 * mm});
            skCircle(sketch, "E26.0.10.14", {"center": v(1.82, 0) * mm, "radius": 0.09 * mm});
            skCircle(sketch, "E26.2.10.14", {"center": v(2.04, -0.13) * mm, "radius": 0.09 * mm});
            skCircle(sketch, "E26.0.10.15", {"center": v(1.82, -0.22) * mm, "radius": 0.09 * mm});
            skCircle(sketch, "E26.2.10.15", {"center": v(2.04, -0.36) * mm, "radius": 0.09 * mm});
            skCircle(sketch, "E26.0.10.16", {"center": v(1.82, -0.45) * mm, "radius": 0.09 * mm});
            skCircle(sketch, "E26.2.10.16", {"center": v(2.04, -0.58) * mm, "radius": 0.09 * mm});
            skCircle(sketch, "E26.0.10.17", {"center": v(1.82, -0.68) * mm, "radius": 0.09 * mm});
            skCircle(sketch, "E26.2.10.17", {"center": v(2.04, -0.8) * mm, "radius": 0.09 * mm});
            skCircle(sketch, "E26.0.10.18", {"center": v(1.82, -0.9) * mm, "radius": 0.09 * mm});
            skCircle(sketch, "E26.2.10.18", {"center": v(2.04, -1.04) * mm, "radius": 0.09 * mm});
            skCircle(sketch, "E26.0.10.19", {"center": v(1.82, -1.13) * mm, "radius": 0.09 * mm});
            skCircle(sketch, "E26.2.10.19", {"center": v(2.04, -1.26) * mm, "radius": 0.09 * mm});
            skCircle(sketch, "E26.0.10.20", {"center": v(1.82, -1.36) * mm, "radius": 0.09 * mm});
            skCircle(sketch, "E26.0.10.21", {"center": v(1.82, -1.59) * mm, "radius": 0.09 * mm});
            skCircle(sketch, "E27.0.11.10", {"center": v(2.27, 0.91) * mm, "radius": 0.09 * mm});
            skCircle(sketch, "E27.0.11.11", {"center": v(2.27, 0.68) * mm, "radius": 0.09 * mm});
            skCircle(sketch, "E27.0.11.12", {"center": v(2.27, 0.46) * mm, "radius": 0.09 * mm});
            skCircle(sketch, "E27.0.11.13", {"center": v(2.27, 0.23) * mm, "radius": 0.09 * mm});
            skCircle(sketch, "E27.0.11.14", {"center": v(2.27, 0) * mm, "radius": 0.09 * mm});
            skCircle(sketch, "E27.0.11.15", {"center": v(2.27, -0.22) * mm, "radius": 0.09 * mm});
            skCircle(sketch, "E27.0.11.16", {"center": v(2.27, -0.45) * mm, "radius": 0.09 * mm});
            skCircle(sketch, "E27.0.11.17", {"center": v(2.27, -0.68) * mm, "radius": 0.09 * mm});
            skCircle(sketch, "E27.0.11.18", {"center": v(2.27, -0.9) * mm, "radius": 0.09 * mm});
            skCircle(sketch, "E28.0.3.22", {"center": v(-1.36, -1.81) * mm, "radius": 0.09 * mm});
            skCircle(sketch, "E28.2.3.22", {"center": v(-1.13, -1.94) * mm, "radius": 0.09 * mm});
            skCircle(sketch, "E28.0.3.23", {"center": v(-1.36, -2.04) * mm, "radius": 0.09 * mm});
            skCircle(sketch, "E28.2.3.23", {"center": v(-1.13, -2.17) * mm, "radius": 0.09 * mm});
            skCircle(sketch, "E28.0.4.22", {"center": v(-0.9, -1.81) * mm, "radius": 0.09 * mm});
            skCircle(sketch, "E28.2.4.22", {"center": v(-0.68, -1.94) * mm, "radius": 0.09 * mm});
            skCircle(sketch, "E28.0.4.23", {"center": v(-0.9, -2.04) * mm, "radius": 0.09 * mm});
            skCircle(sketch, "E28.2.4.23", {"center": v(-0.68, -2.17) * mm, "radius": 0.09 * mm});
            skCircle(sketch, "E28.0.4.24", {"center": v(-0.9, -2.27) * mm, "radius": 0.09 * mm});
            skCircle(sketch, "E28.0.5.22", {"center": v(-0.45, -1.81) * mm, "radius": 0.09 * mm});
            skCircle(sketch, "E28.2.5.22", {"center": v(-0.23, -1.94) * mm, "radius": 0.09 * mm});
            skCircle(sketch, "E28.0.5.23", {"center": v(-0.45, -2.04) * mm, "radius": 0.09 * mm});
            skCircle(sketch, "E28.2.5.23", {"center": v(-0.23, -2.17) * mm, "radius": 0.09 * mm});
            skCircle(sketch, "E28.0.5.24", {"center": v(-0.45, -2.27) * mm, "radius": 0.09 * mm});
            skCircle(sketch, "E28.2.5.24", {"center": v(-0.23, -2.4) * mm, "radius": 0.09 * mm});
            skCircle(sketch, "E28.0.6.22", {"center": v(0, -1.81) * mm, "radius": 0.09 * mm});
            skCircle(sketch, "E28.2.6.22", {"center": v(0.23, -1.94) * mm, "radius": 0.09 * mm});
            skCircle(sketch, "E28.0.6.23", {"center": v(0, -2.04) * mm, "radius": 0.09 * mm});
            skCircle(sketch, "E28.2.6.23", {"center": v(0.23, -2.17) * mm, "radius": 0.09 * mm});
            skCircle(sketch, "E28.0.6.24", {"center": v(0, -2.27) * mm, "radius": 0.09 * mm});
            skCircle(sketch, "E28.2.6.24", {"center": v(0.23, -2.4) * mm, "radius": 0.09 * mm});
            skCircle(sketch, "E28.0.7.22", {"center": v(0.45, -1.81) * mm, "radius": 0.09 * mm});
            skCircle(sketch, "E28.2.7.22", {"center": v(0.68, -1.94) * mm, "radius": 0.09 * mm});
            skCircle(sketch, "E28.0.7.23", {"center": v(0.45, -2.04) * mm, "radius": 0.09 * mm});
            skCircle(sketch, "E28.2.7.23", {"center": v(0.68, -2.17) * mm, "radius": 0.09 * mm});
            skCircle(sketch, "E28.0.7.24", {"center": v(0.45, -2.27) * mm, "radius": 0.09 * mm});
            skCircle(sketch, "E28.0.8.22", {"center": v(0.9, -1.81) * mm, "radius": 0.09 * mm});
            skCircle(sketch, "E28.2.8.22", {"center": v(1.14, -1.94) * mm, "radius": 0.09 * mm});
            skCircle(sketch, "E28.0.8.23", {"center": v(0.9, -2.04) * mm, "radius": 0.09 * mm});
            skCircle(sketch, "E28.2.8.23", {"center": v(1.14, -2.17) * mm, "radius": 0.09 * mm});
            skCircle(sketch, "E28.0.8.24", {"center": v(0.9, -2.27) * mm, "radius": 0.09 * mm});
            skCircle(sketch, "E28.0.9.22", {"center": v(1.36, -1.81) * mm, "radius": 0.09 * mm});
            skCircle(sketch, "E28.0.9.23", {"center": v(1.36, -2.04) * mm, "radius": 0.09 * mm});
            skCircle(sketch, "E29.0", {"center": v(0, 0) * mm, "radius": 2.5 * mm, "construction": true});
            skSolve(sketch);
        }
        {
            var Q0;
            Q0=qSketchRegion(id+"F3",true);
            extrude(context, id + "F4", {"entities" : qUnion([Q0]), "operationType" : NewBodyOperationType.REMOVE, "endBound" : BoundingType.THROUGH_ALL, "oppositeDirection" : true, "depth" : 25 * mm});
        }
    });
